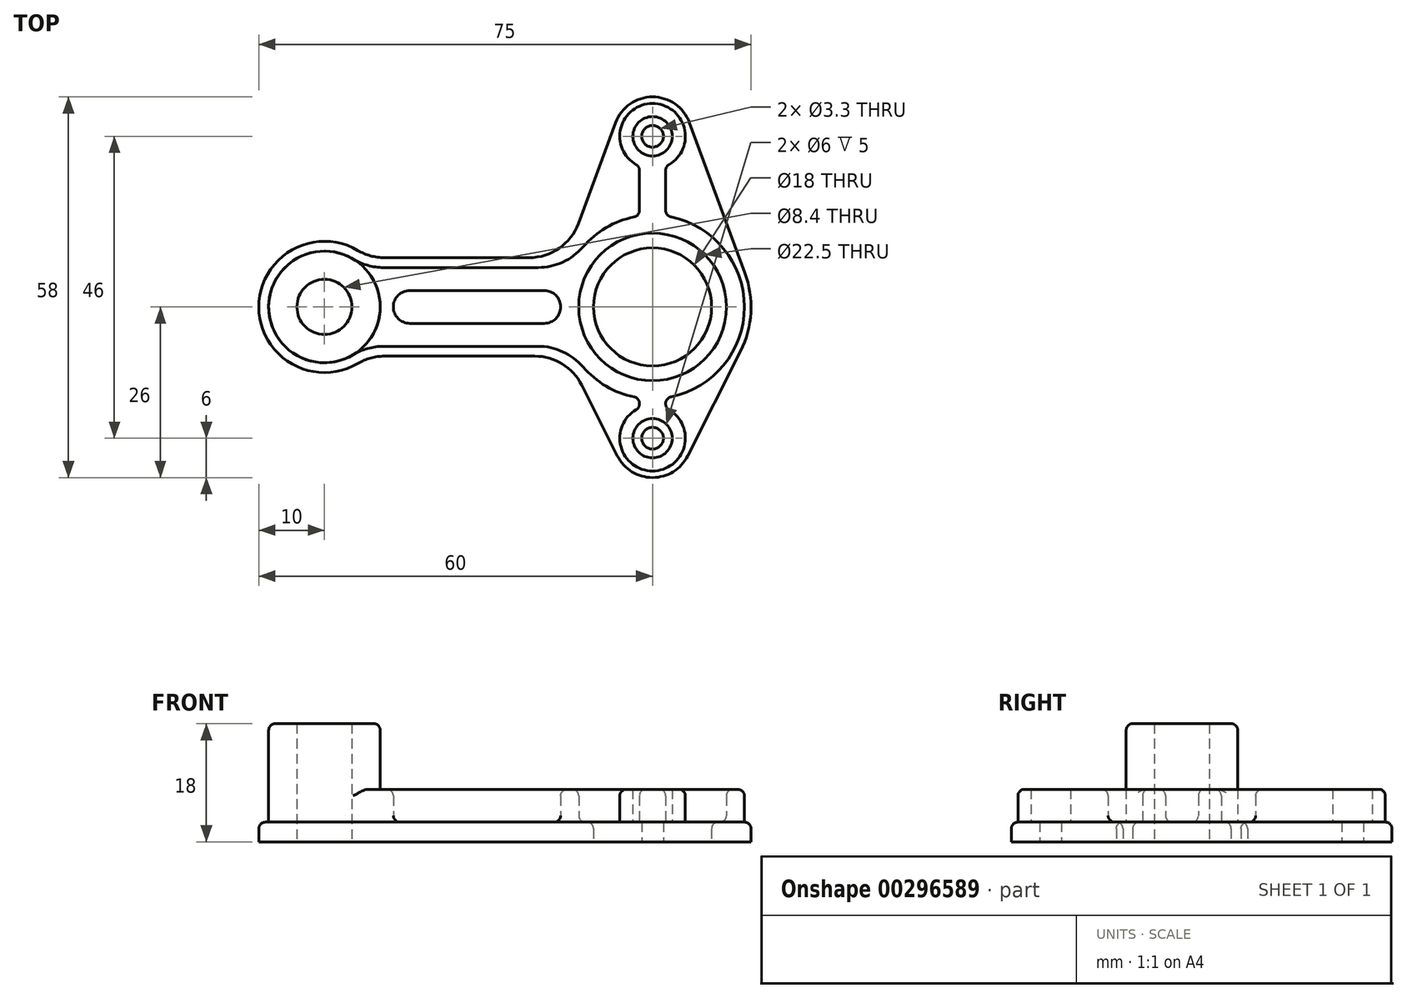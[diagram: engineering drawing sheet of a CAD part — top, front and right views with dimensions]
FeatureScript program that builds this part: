
annotation { "Feature Type Name" : "Feature", "Feature Type Description" : "" }
export const myFeature = defineFeature(function(context is Context, id is Id, definition is map)
    precondition{}
    {
        {
            var Q0;
            Q0=qCreatedBy(makeId("Top.planeOp"),FACE);
            var sketch = newSketch(context, id + "F0", { "sketchPlane" : qUnion([Q0])});
            skCircle(sketch, "E0", {"center": v(0, 0) * mm, "radius": 9 * mm});
            skArc(sketch, "E1", {"start": v(-14.07, 5.2) * mm, "mid": v(-14.98, -0.85) * mm, "end": v(-13.4, -6.75) * mm, "construction": true});
            skLineSegment(sketch, "E2", {"start": v(0, 0) * mm, "end": v(0, -20) * mm, "construction": true});
            skCircle(sketch, "E3", {"center": v(0, -20) * mm, "radius": 1.65 * mm});
            skLineSegment(sketch, "E4", {"start": v(0, 0) * mm, "end": v(0, 26) * mm, "construction": true});
            skCircle(sketch, "E5", {"center": v(0, 26) * mm, "radius": 1.65 * mm});
            skArc(sketch, "E6", {"start": v(5.63, 28.08) * mm, "mid": v(0, 32) * mm, "end": v(-5.63, 28.08) * mm});
            skArc(sketch, "E7", {"start": v(-5.36, -22.7) * mm, "mid": v(0, -26) * mm, "end": v(5.36, -22.7) * mm});
            skLineSegment(sketch, "E8", {"start": v(-5.63, 28.08) * mm, "end": v(-11.3, 12.73) * mm});
            skLineSegment(sketch, "E9", {"start": v(-10.8, -11.9) * mm, "end": v(-5.36, -22.7) * mm});
            skLineSegment(sketch, "E10", {"start": v(5.36, -22.7) * mm, "end": v(13.4, -6.75) * mm});
            skLineSegment(sketch, "E11", {"start": v(5.63, 28.08) * mm, "end": v(14.07, 5.2) * mm});
            skArc(sketch, "E12.trimOffspring", {"start": v(13.4, -6.75) * mm, "mid": v(14.98, -0.85) * mm, "end": v(14.07, 5.2) * mm});
            skLineSegment(sketch, "E13", {"start": v(0, 0) * mm, "end": v(-50, 0) * mm, "construction": true});
            skCircle(sketch, "E14", {"center": v(-50, 0) * mm, "radius": 4.2 * mm});
            skArc(sketch, "E15", {"start": v(-44.92, 8.61) * mm, "mid": v(-60, 0) * mm, "end": v(-44.92, -8.61) * mm});
            skLineSegment(sketch, "E16.0", {"start": v(-18.8, 7.5) * mm, "end": v(-40.85, 7.5) * mm});
            skLineSegment(sketch, "E17.0", {"start": v(-17.94, -7.5) * mm, "end": v(-40.85, -7.5) * mm});
            skPoint(sketch, "E18.visualSharp", {"position": v(-13.22, 7.5) * mm});
            skArc(sketch, "E18.filletArc", {"start": v(-18.8, 7.5) * mm, "mid": v(-14.22, 8.94) * mm, "end": v(-11.3, 12.73) * mm});
            skPoint(sketch, "E19.visualSharp", {"position": v(-13.02, -7.5) * mm});
            skArc(sketch, "E19.filletArc", {"start": v(-10.8, -11.9) * mm, "mid": v(-13.75, -8.69) * mm, "end": v(-17.94, -7.5) * mm});
            skPoint(sketch, "E20.visualSharp", {"position": v(-43.39, -7.5) * mm});
            skArc(sketch, "E20.filletArc", {"start": v(-40.85, -7.5) * mm, "mid": v(-42.96, -7.78) * mm, "end": v(-44.92, -8.61) * mm});
            skPoint(sketch, "E21.visualSharp", {"position": v(-43.39, 7.5) * mm});
            skArc(sketch, "E21.filletArc", {"start": v(-44.92, 8.61) * mm, "mid": v(-42.96, 7.78) * mm, "end": v(-40.85, 7.5) * mm});
            skSolve(sketch);
        }
        {
            var Q0;
            Q0 = qSketchRegion(id + "F0", true);
            extrude(context, id + "F1", {"entities" : qUnion([Q0]), "depth" : 3 * mm});
        }
        {
            var Q0;
            Q0=makeQuery(id+"F1.opExtrude","CAP_FACE",FACE,{"disambiguationData":[OSD([sQuery(id+"F0.wireOp",EDGE,"E0"),sQuery(id+"F0.wireOp",EDGE,"E1"),sQuery(id+"F0.wireOp",EDGE,"E3"),sQuery(id+"F0.wireOp",EDGE,"E5"),sQuery(id+"F0.wireOp",EDGE,"E6"),sQuery(id+"F0.wireOp",EDGE,"E7"),sQuery(id+"F0.wireOp",EDGE,"E8"),sQuery(id+"F0.wireOp",EDGE,"E9"),sQuery(id+"F0.wireOp",EDGE,"E10"),sQuery(id+"F0.wireOp",EDGE,"E11"),sQuery(id+"F0.wireOp",EDGE,"E12.trimOffspring")])],"isStart":false});
            var sketch = newSketch(context, id + "F2", { "sketchPlane" : qUnion([Q0])});
            skArc(sketch, "E22", {"start": v(2.5, 21.67) * mm, "mid": v(0, 31) * mm, "end": v(-2.5, 21.67) * mm});
            skCircle(sketch, "E23", {"center": v(0, 0) * mm, "radius": 11.25 * mm});
            skArc(sketch, "E24", {"start": v(-2.8, 13.72) * mm, "mid": v(-7.09, 12.07) * mm, "end": v(-10.61, 9.13) * mm});
            skLineSegment(sketch, "E25", {"start": v(0, 26) * mm, "end": v(0, 0) * mm, "construction": true});
            skLineSegment(sketch, "E26", {"start": v(0, -20) * mm, "end": v(0, 0) * mm, "construction": true});
            skArc(sketch, "E27.trimOffspring", {"start": v(2.8, -13.72) * mm, "mid": v(14, 0) * mm, "end": v(2.8, 13.72) * mm});
            skArc(sketch, "E28", {"start": v(-2.5, -15.67) * mm, "mid": v(0, -25) * mm, "end": v(2.5, -15.67) * mm});
            skLineSegment(sketch, "E29.0", {"start": v(2, -14.8) * mm, "end": v(2, -14.7) * mm});
            skLineSegment(sketch, "E30.0", {"start": v(-2, -14.8) * mm, "end": v(-2, -14.7) * mm});
            skLineSegment(sketch, "E31.0", {"start": v(-2, 20.8) * mm, "end": v(-2, 14.7) * mm});
            skLineSegment(sketch, "E32.0", {"start": v(2, 20.8) * mm, "end": v(2, 14.7) * mm});
            skPoint(sketch, "E33.visualSharp", {"position": v(2, 13.86) * mm});
            skArc(sketch, "E33.filletArc", {"start": v(2, 14.7) * mm, "mid": v(2.23, 14.06) * mm, "end": v(2.8, 13.72) * mm});
            skPoint(sketch, "E34.visualSharp", {"position": v(2, -15.42) * mm});
            skArc(sketch, "E34.filletArc", {"start": v(2, -14.8) * mm, "mid": v(2.13, -15.3) * mm, "end": v(2.5, -15.67) * mm});
            skPoint(sketch, "E35.visualSharp", {"position": v(2, -13.86) * mm});
            skArc(sketch, "E35.filletArc", {"start": v(2.8, -13.72) * mm, "mid": v(2.23, -14.06) * mm, "end": v(2, -14.7) * mm});
            skPoint(sketch, "E36.visualSharp", {"position": v(-2, -13.86) * mm});
            skArc(sketch, "E36.filletArc", {"start": v(-2, -14.7) * mm, "mid": v(-2.23, -14.06) * mm, "end": v(-2.8, -13.72) * mm});
            skPoint(sketch, "E37.visualSharp", {"position": v(-2, -15.42) * mm});
            skArc(sketch, "E37.filletArc", {"start": v(-2.5, -15.67) * mm, "mid": v(-2.13, -15.3) * mm, "end": v(-2, -14.8) * mm});
            skPoint(sketch, "E38.visualSharp", {"position": v(2, 21.42) * mm});
            skArc(sketch, "E38.filletArc", {"start": v(2.5, 21.67) * mm, "mid": v(2.13, 21.3) * mm, "end": v(2, 20.8) * mm});
            skPoint(sketch, "E39.visualSharp", {"position": v(-2, 21.42) * mm});
            skArc(sketch, "E39.filletArc", {"start": v(-2, 20.8) * mm, "mid": v(-2.13, 21.3) * mm, "end": v(-2.5, 21.67) * mm});
            skPoint(sketch, "E40.visualSharp", {"position": v(-2, 13.86) * mm});
            skArc(sketch, "E40.filletArc", {"start": v(-2.8, 13.72) * mm, "mid": v(-2.23, 14.06) * mm, "end": v(-2, 14.7) * mm});
            skCircle(sketch, "E41", {"center": v(0, -20) * mm, "radius": 3 * mm});
            skCircle(sketch, "E42", {"center": v(0, 26) * mm, "radius": 3 * mm});
            skCircle(sketch, "E43", {"center": v(-50, 0) * mm, "radius": 4.2 * mm});
            skArc(sketch, "E44", {"start": v(-45.62, 7.29) * mm, "mid": v(-58.5, 0) * mm, "end": v(-45.62, -7.29) * mm});
            skLineSegment(sketch, "E45", {"start": v(-50, 0) * mm, "end": v(0, 0) * mm, "construction": true});
            skLineSegment(sketch, "E46.0", {"start": v(-40.99, -6) * mm, "end": v(-17.44, -6) * mm});
            skLineSegment(sketch, "E47.0", {"start": v(-40.99, 6) * mm, "end": v(-17.44, 6) * mm});
            skLineSegment(sketch, "E48.0", {"start": v(-37, 2.5) * mm, "end": v(-16.5, 2.5) * mm});
            skLineSegment(sketch, "E49.0", {"start": v(-37, -2.5) * mm, "end": v(-16.5, -2.5) * mm});
            skArc(sketch, "E50", {"start": v(-37, 2.5) * mm, "mid": v(-39.5, 0) * mm, "end": v(-37, -2.5) * mm});
            skArc(sketch, "E51", {"start": v(-16.5, -2.5) * mm, "mid": v(-14, 0) * mm, "end": v(-16.5, 2.5) * mm});
            skArc(sketch, "E52.trimOffspring", {"start": v(-10.61, -9.13) * mm, "mid": v(-7.09, -12.07) * mm, "end": v(-2.8, -13.72) * mm});
            skPoint(sketch, "E53.visualSharp", {"position": v(-43.98, -6) * mm});
            skArc(sketch, "E53.filletArc", {"start": v(-40.99, -6) * mm, "mid": v(-43.4, -6.33) * mm, "end": v(-45.62, -7.29) * mm});
            skPoint(sketch, "E54.visualSharp", {"position": v(-43.98, 6) * mm});
            skArc(sketch, "E54.filletArc", {"start": v(-45.62, 7.29) * mm, "mid": v(-43.4, 6.33) * mm, "end": v(-40.99, 6) * mm});
            skPoint(sketch, "E55.visualSharp", {"position": v(-12.65, 6) * mm});
            skArc(sketch, "E55.filletArc", {"start": v(-17.44, 6) * mm, "mid": v(-13.68, 6.82) * mm, "end": v(-10.61, 9.13) * mm});
            skPoint(sketch, "E56.visualSharp", {"position": v(-12.65, -6) * mm});
            skArc(sketch, "E56.filletArc", {"start": v(-10.61, -9.13) * mm, "mid": v(-13.68, -6.82) * mm, "end": v(-17.44, -6) * mm});
            skSolve(sketch);
        }
        {
            var Q0;
            Q0 = qSketchRegion(id + "F2", true);
            extrude(context, id + "F3", {"entities" : qUnion([Q0]), "operationType" : NewBodyOperationType.ADD, "depth" : 5 * mm});
        }
        {
            var Q0;
            Q0=makeQuery(id+"F3.opExtrude","CAP_FACE",FACE,{"disambiguationData":[OSD([sQuery(id+"F2.wireOp",EDGE,"E22"),sQuery(id+"F2.wireOp",EDGE,"E23"),sQuery(id+"F2.wireOp",EDGE,"E24"),sQuery(id+"F2.wireOp",EDGE,"E27.trimOffspring"),sQuery(id+"F2.wireOp",EDGE,"E28"),sQuery(id+"F2.wireOp",EDGE,"E29.0"),sQuery(id+"F2.wireOp",EDGE,"E30.0"),sQuery(id+"F2.wireOp",EDGE,"E31.0"),sQuery(id+"F2.wireOp",EDGE,"E32.0"),sQuery(id+"F2.wireOp",EDGE,"E33.filletArc"),sQuery(id+"F2.wireOp",EDGE,"E34.filletArc"),sQuery(id+"F2.wireOp",EDGE,"E35.filletArc"),sQuery(id+"F2.wireOp",EDGE,"E36.filletArc"),sQuery(id+"F2.wireOp",EDGE,"E37.filletArc"),sQuery(id+"F2.wireOp",EDGE,"E38.filletArc"),sQuery(id+"F2.wireOp",EDGE,"E39.filletArc"),sQuery(id+"F2.wireOp",EDGE,"E40.filletArc"),sQuery(id+"F2.wireOp",EDGE,"E41"),sQuery(id+"F2.wireOp",EDGE,"E42"),sQuery(id+"F2.wireOp",EDGE,"E43"),sQuery(id+"F2.wireOp",EDGE,"E44"),sQuery(id+"F2.wireOp",EDGE,"E46.0"),sQuery(id+"F2.wireOp",EDGE,"E47.0"),sQuery(id+"F2.wireOp",EDGE,"E48.0"),sQuery(id+"F2.wireOp",EDGE,"E49.0"),sQuery(id+"F2.wireOp",EDGE,"E50"),sQuery(id+"F2.wireOp",EDGE,"E51"),sQuery(id+"F2.wireOp",EDGE,"E52.trimOffspring"),sQuery(id+"F2.wireOp",EDGE,"E53.filletArc"),sQuery(id+"F2.wireOp",EDGE,"E54.filletArc"),sQuery(id+"F2.wireOp",EDGE,"E55.filletArc"),sQuery(id+"F2.wireOp",EDGE,"E56.filletArc")])],"isStart":false});
            var sketch = newSketch(context, id + "F4", { "sketchPlane" : qUnion([Q0])});
            skCircle(sketch, "E57", {"center": v(-50, 0) * mm, "radius": 4.2 * mm});
            skCircle(sketch, "E58", {"center": v(-50, 0) * mm, "radius": 8.5 * mm});
            skSolve(sketch);
        }
        {
            var Q0;
            Q0 = qSketchRegion(id + "F4", true);
            extrude(context, id + "F5", {"entities" : qUnion([Q0]), "operationType" : NewBodyOperationType.ADD, "depth" : 10 * mm});
        }
        {
            var Q0;
            Q0=makeQuery(id+"F1.opExtrude","CAP_EDGE",EDGE,{"disambiguationData":[OSD([sQuery(id+"F0.wireOp",EDGE,"E0")])],"isStart":false});
            var Q1;
            Q1=makeQuery(id+"F3.opExtrude","CAP_EDGE",EDGE,{"disambiguationData":[OSD([sQuery(id+"F2.wireOp",EDGE,"E23")])],"isStart":false});
            var Q2;
            Q2=makeQuery(id+"F3.opExtrude","CAP_EDGE",EDGE,{"disambiguationData":[OSD([sQuery(id+"F2.wireOp",EDGE,"E23")])],"isStart":true});
            var Q3;
            Q3=makeQuery(id+"F3.opExtrude","CAP_EDGE",EDGE,{"disambiguationData":[OSD([sQuery(id+"F2.wireOp",EDGE,"E27.trimOffspring")])],"isStart":false});
            var Q4;
            Q4=makeQuery(id+"F1.opExtrude","CAP_EDGE",EDGE,{"disambiguationData":[OSD([sQuery(id+"F0.wireOp",EDGE,"E9")])],"isStart":false});
            var Q5;
            Q5=makeQuery(id+"F3.opExtrude","CAP_EDGE",EDGE,{"disambiguationData":[OSD([sQuery(id+"F2.wireOp",EDGE,"E48.0")])],"isStart":true});
            var Q6;
            Q6=makeQuery(id+"F3.opExtrude","CAP_EDGE",EDGE,{"disambiguationData":[OSD([sQuery(id+"F2.wireOp",EDGE,"E48.0")])],"isStart":false});
            fillet(context, id + "F6", {"entities" : qUnion([Q0, Q1, Q2, Q3, Q4, Q5, Q6]), "radius" : 1 * mm, "tangentPropagation" : true, "allowEdgeOverflow" : false});
        }
        {
            var Q0;
            Q0=makeQuery(id+"F3.opExtrude","CAP_EDGE",EDGE,{"disambiguationData":[OSD([sQuery(id+"F2.wireOp",EDGE,"E24")])],"isStart":true});
            var Q1;
            Q1=makeQuery(id+"F5.opExtrude","CAP_EDGE",EDGE,{"disambiguationData":[OSD([sQuery(id+"F4.wireOp",EDGE,"E58")])],"isStart":true});
            var Q2;
            Q2=makeQuery(id+"F5.opExtrude","CAP_EDGE",EDGE,{"disambiguationData":[OSD([sQuery(id+"F4.wireOp",EDGE,"E58")])],"isStart":false});
            fillet(context, id + "F7", {"entities" : qUnion([Q0, Q1, Q2]), "radius" : 1 * mm, "tangentPropagation" : true, "allowEdgeOverflow" : false});
        }
    });
